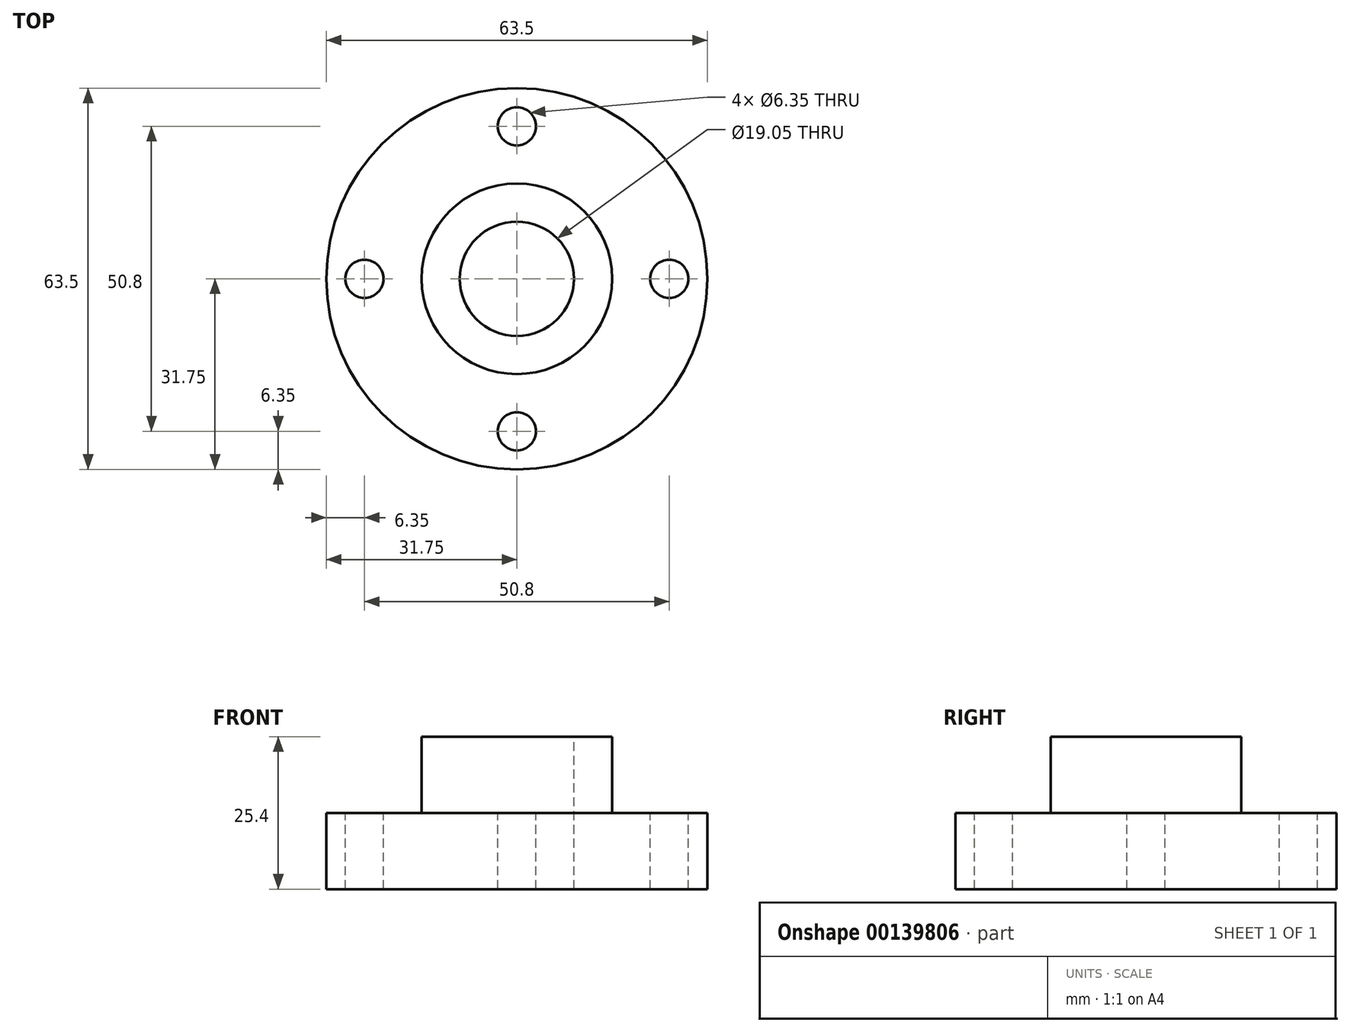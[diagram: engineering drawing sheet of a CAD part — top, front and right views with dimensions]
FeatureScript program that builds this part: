
annotation { "Feature Type Name" : "Feature", "Feature Type Description" : "" }
export const myFeature = defineFeature(function(context is Context, id is Id, definition is map)
    precondition{}
    {
        {
            var Q0;
            Q0=qCreatedBy(makeId("Top.planeOp"),FACE);
            var sketch = newSketch(context, id + "F0", { "sketchPlane" : qUnion([Q0])});
            skCircle(sketch, "E0", {"center": v(0, 0) * mm, "radius": 31.75 * mm});
            skCircle(sketch, "E1", {"center": v(0, 0) * mm, "radius": 15.88 * mm});
            skCircle(sketch, "E2", {"center": v(0, 0) * mm, "radius": 9.53 * mm});
            skCircle(sketch, "E3", {"center": v(0, 0) * mm, "radius": 25.4 * mm, "construction": true});
            skCircle(sketch, "E4", {"center": v(0, 25.4) * mm, "radius": 3.18 * mm});
            skCircle(sketch, "E5.1.0", {"center": v(-25.4, 0) * mm, "radius": 3.18 * mm});
            skCircle(sketch, "E5.2.0", {"center": v(0, -25.4) * mm, "radius": 3.18 * mm});
            skCircle(sketch, "E5.3.0", {"center": v(25.4, 0) * mm, "radius": 3.18 * mm});
            skSolve(sketch);
        }
        {
            var Q0;
            Q0=makeQuery(id+"F0.imprint","IMPRINT",FACE,{"disambiguationData":[TD([[makeQuery(id+"F0.imprint","IMPRINT",EDGE,{"derivedFrom":sQuery(id+"F0.wireOp",EDGE,"E0")}),1.0]])]});
            var Q1;
            Q1=makeQuery(id+"F0.imprint","IMPRINT",FACE,{"disambiguationData":[TD([[makeQuery(id+"F0.imprint","IMPRINT",EDGE,{"derivedFrom":sQuery(id+"F0.wireOp",EDGE,"E1")}),1.0]])]});
            extrude(context, id + "F1", {"entities" : qUnion([Q0, Q1]), "oppositeDirection" : true, "depth" : 12.7 * mm});
        }
        {
            var Q0;
            Q0=makeQuery(id+"F0.imprint","IMPRINT",FACE,{"disambiguationData":[TD([[makeQuery(id+"F0.imprint","IMPRINT",EDGE,{"derivedFrom":sQuery(id+"F0.wireOp",EDGE,"E1")}),1.0]])]});
            extrude(context, id + "F2", {"entities" : qUnion([Q0]), "operationType" : NewBodyOperationType.ADD, "depth" : 12.7 * mm});
        }
    });
